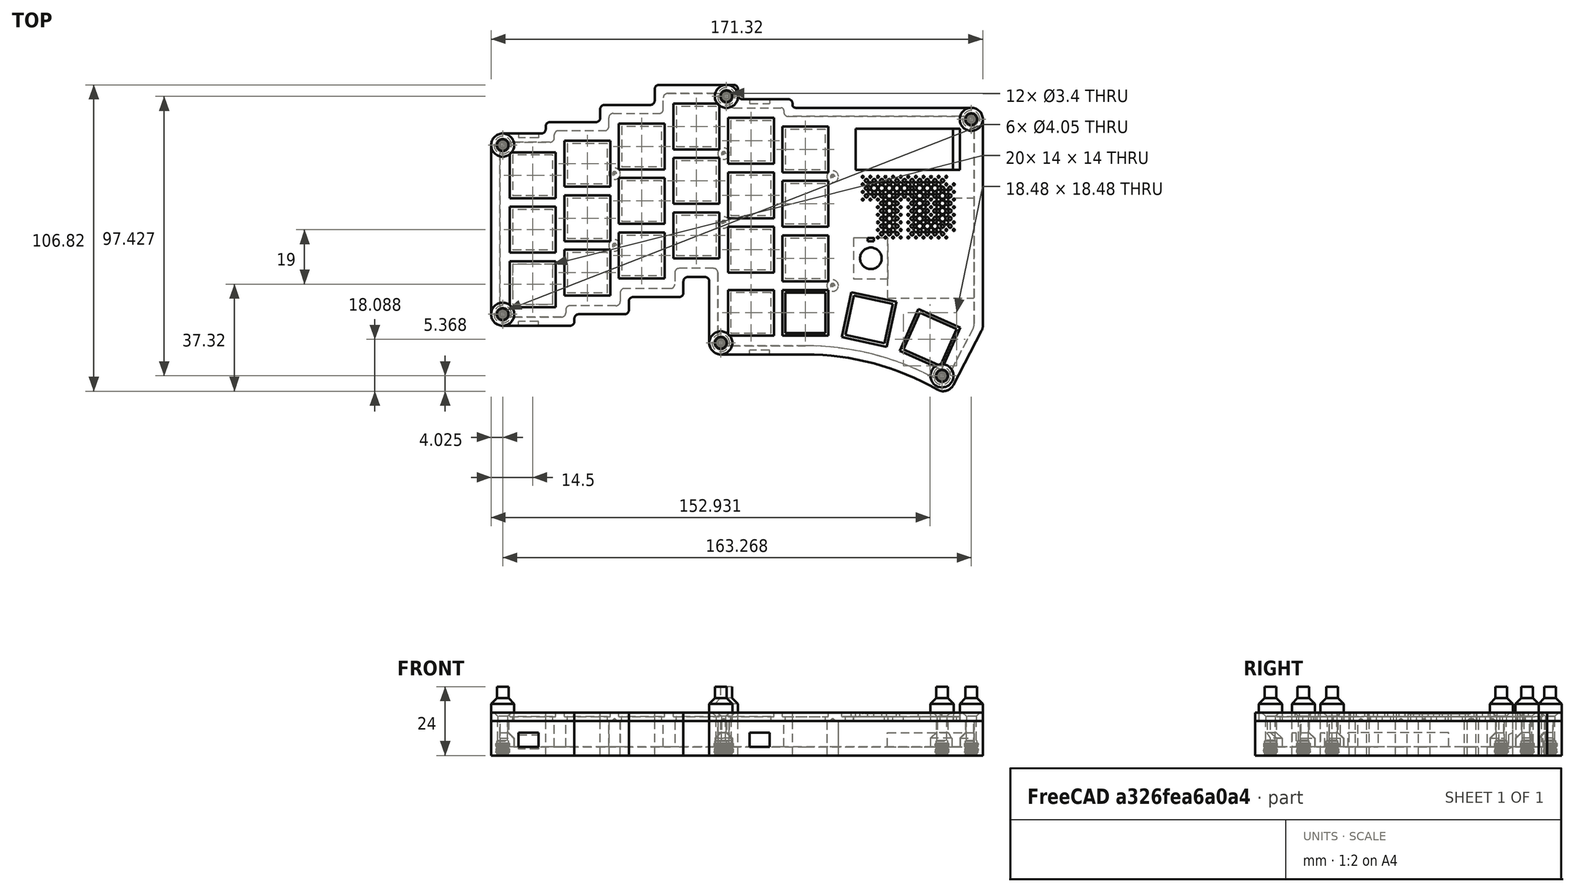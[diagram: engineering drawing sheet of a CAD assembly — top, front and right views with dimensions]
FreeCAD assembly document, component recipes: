
FREECAD ASSEMBLY — COMPONENT RECIPES ("LeftFrameTop")

This assembly document has 8 components, labeled P0..P7 below (a component is one placed body or linked part). 6 of them carry a construction recipe — the FreeCAD feature program that regenerates the part from scratch, quoted from this document or its linked companion documents; the rest are supplied as boundary geometry only. No exploded tour is included for this assembly.
COMPONENT P0 — recipe-attached ("SwitchPocket", modeled in this document).
Construction recipe (the document's own serialized feature program — sketch geometry with constraints, then the solid features built on it; lengths are millimeters unless a unit is written):

FEATURE [PartDesign::SubShapeBinder] Binder  label="FrameBorderBinder"
  BindCopyOnChange = 0
  BindMode = 0
  ClaimChildren = false
  Context = -> Body001 [Binder.]
  Fuse = false
  MakeFace = true
  OffsetFill = false
  OffsetIntersection = false
  OffsetJoinType = 0
  OffsetOpenResult = false
  PartialLoad = false
  Refine = true
  Relative = true
  Support = -> [Sketch002]
  _Version = 2
FEATURE [PartDesign::Pad] Pad
  Direction = (0,0,1)
  Length = 3
  Length2 = 10
  Profile = -> Binder
  Refine = true
  Suppressed = false
  Type = 0
  expr: Length = <<Config>>#<<Vars>>.PlateThickness
FEATURE [PartDesign::Fillet] Fillet
  Base = -> Pad [Edge38,Edge41,Edge44,Edge47,Edge50,Edge53,Edge56,Edge5,Edge11,Edge14,Edge8,Edge20,Edge17,Edge23,Edge26,Edge29]
  BaseFeature = -> Pad
  Radius = 1.5
  Refine = true
  SupportTransform = false
  Suppressed = false
  UseAllEdges = false
  expr: Radius = <<Config>>#<<Vars>>.MediumFillet
FEATURE [PartDesign::Fillet] Fillet001
  Base = -> Fillet [Edge119,Edge92,Edge88,Edge86,Edge46,Edge117]
  BaseFeature = -> Fillet
  Radius = 4
  Refine = true
  SupportTransform = false
  Suppressed = false
  UseAllEdges = false
  expr: Radius = <<Config>>#<<Vars>>.BigFillet
FEATURE [PartDesign::Fillet] Fillet002
  Base = -> Fillet001 [Edge48]
  BaseFeature = -> Fillet001
  Radius = 1
  Refine = true
  SupportTransform = false
  Suppressed = false
  UseAllEdges = false
  expr: Radius = <<Config>>#<<Vars>>.LittleFillet
FEATURE [PartDesign::Boolean] Boolean
  BaseFeature = -> Fillet002
  Group = -> [Array]
  Refine = true
  Suppressed = false
  Type = 1
  UsePlacement = true
FEATURE [PartDesign::Boolean] Boolean001
  BaseFeature = -> Boolean
  Group = -> [Binder002]
  Refine = true
  Suppressed = false
  Type = 1
  UsePlacement = true
FEATURE [PartDesign::Boolean] Boolean002
  BaseFeature = -> Boolean001
  Group = -> [Binder003]
  Refine = true
  Suppressed = false
  Type = 1
  UsePlacement = true
FEATURE [PartDesign::Boolean] Boolean003
  BaseFeature = -> Boolean002
  Group = -> [Binder004]
  Refine = true
  Suppressed = false
  Type = 1
  UsePlacement = true
FEATURE [PartDesign::SubShapeBinder] Binder009  label="M3HoleGeometryBinder"
  BindCopyOnChange = 0
  BindMode = 0
  ClaimChildren = false
  Context = -> Body001 [Binder009.]
  Fuse = false
  MakeFace = true
  OffsetFill = false
  OffsetIntersection = false
  OffsetJoinType = 0
  OffsetOpenResult = false
  PartialLoad = false
  Placement = pos=(0,0,3) rot=(0,0,1;0rad)
  Refine = true
  Relative = true
  Support = -> [PointArray003]
  _Version = 2
  expr: .Placement.Base.z = <<Config>>#<<Vars>>.PlateThickness
FEATURE [PartDesign::Hole] Hole
  BaseFeature = -> Boolean003
  CustomThreadClearance = 0
  Depth = 25
  DepthType = 0
  Diameter = 3.4
  DrillForDepth = false
  DrillPoint = 1
  DrillPointAngle = 118
  HoleCutCountersinkAngle = 90
  HoleCutCustomValues = false
  HoleCutDepth = 0
  HoleCutDiameter = 6.1
  HoleCutType = 2
  ModelThread = false
  Profile = -> Binder009
  Refine = true
  Suppressed = false
  Tapered = false
  TaperedAngle = 90
  ThreadClass = 0
  ThreadDepth = 25
  ThreadDepthType = 0
  ThreadDirection = 0
  ThreadFit = 0
  ThreadSize = 9
  ThreadType = 1
  Threaded = false
  UseCustomThreadClearance = false
FEATURE [PartDesign::Boolean] Boolean006
  BaseFeature = -> Hole
  Group = -> [Binder012]
  Refine = true
  Suppressed = false
  Type = 1
  UsePlacement = true
FEATURE [PartDesign::SubShapeBinder] Binder015
  BindCopyOnChange = 0
  BindMode = 0
  ClaimChildren = false
  Context = -> Body001 [Binder015.]
  Fuse = false
  MakeFace = true
  OffsetFill = false
  OffsetIntersection = false
  OffsetJoinType = 0
  OffsetOpenResult = false
  PartialLoad = false
  Placement = pos=(125.5,55.9,3) rot=(0,0,1;0rad)
  Refine = true
  Relative = true
  Support = -> [<external ../logo/Logo.FCStd>#Sketch]
  _Version = 2
  expr: .Placement.Base.z = <<Config>>#<<Vars>>.PlateThickness
FEATURE [PartDesign::Pocket] Pocket
  BaseFeature = -> Boolean006
  Direction = (0,0,-1)
  Length = 0.5
  Length2 = 5
  Profile = -> Binder015
  Refine = true
  Suppressed = false
  Type = 0
FEATURE [PartDesign::Body] Body001  label="FrameTop"
  AllowCompound = false
  Group = -> [Pad,Fillet,Fillet001,Fillet002,Binder,Boolean,Boolean001,Boolean002,Boolean003,Binder009,Hole,Boolean006,Binder015,Pocket]
  Origin = -> Origin001
  Tip = -> Pocket
COMPONENT P1 — same part as P0; its construction recipe is shown at P0.
COMPONENT P2 — geometry summary ("nice!nano v2 v1"; no construction recipe available for this part):
  bounding box: 34.2 x 17.8 x 3.3 mm
  tessellated surface: 61,186 triangles
  volume: 870 mm^3 (44% of its bounding box)
COMPONENT P3 — geometry summary ("EC11B-SW-Vert-F"; no construction recipe available for this part):
  bounding box: 25.4 x 14.9 x 12.0 mm
  tessellated surface: 43,648 triangles
  volume: 1468 mm^3 (32% of its bounding box)
COMPONENT P4 — recipe-attached ("RotaryPocket", a linked part whose construction recipe lives in a companion FreeCAD document of the same project; that document's serialized recipe follows).
Construction recipe (the companion document, serialized — sketch geometry with constraints, then the solid features built on it; lengths are millimeters unless a unit is written):

FCSTD DOCUMENT  (FreeCAD 1.0R39319 (Git))
Label: SwitchHoleNegative
License: All rights reserved
LicenseURL: https://en.wikipedia.org/wiki/All_rights_reserved
objects: Sketcher::SketchObject×7, PartDesign::Pad×7, PartDesign::Body×3, App::Link×1
note: 38 computed .brp shape members not serialized (recipe doc carries the construction recipe); baked Part::Feature solids carry a one-line shape summary decoded from their .brp
EXTERNAL_REF file=Config.FCStd obj=VarSet
EXTERNAL_REF file=lib/ec11.FCStd obj=EC11B_SW_Vert_F

FEATURE [Sketcher::SketchObject] Sketch001
  ArcFitTolerance = 1e-06
  AttachmentSupport = -> [XY_Plane003]
  FullyConstrained = true
  MakeInternals = false
  MapMode = 5
  expr: Constraints[8] = <<Config>>#<<Vars>>.SwitchHoleTotal
  expr: Constraints[9] = <<Config>>#<<Vars>>.SwitchHoleTotal
  sketch-geometry (4):
    g0: LineSegment StartX=7.025 StartY=-7.025 StartZ=0 EndX=7.025 EndY=7.025 EndZ=0
    g1: LineSegment StartX=7.025 StartY=7.025 StartZ=0 EndX=-7.025 EndY=7.025 EndZ=0
    g2: LineSegment StartX=-7.025 StartY=7.025 StartZ=0 EndX=-7.025 EndY=-7.025 EndZ=0
    g3: LineSegment StartX=-7.025 StartY=-7.025 StartZ=0 EndX=7.025 EndY=-7.025 EndZ=0
  constraints (11):
    c: Coincident(g0,g1)
    c: Coincident(g1,g2)
    c: Coincident(g2,g3)
    c: Coincident(g3,g0)
    c: Vertical(g0)
    c: Vertical(g2)
    c: Horizontal(g1)
    c: Horizontal(g3)
    c: DistanceX(g1,g1) = 14.05
    c: DistanceY(g2,g2) = 14.05
    c: Symmetric(g1,g0,g-1)
FEATURE [PartDesign::Pad] Pad001
  Direction = (0,0,1)
  Length = 1.5
  Length2 = 10
  Profile = -> Sketch001
  ReferenceAxis = -> Sketch001 [N_Axis]
  Refine = true
  Suppressed = false
  Type = 0
  expr: Length = <<Config>>#<<Vars>>.SwitchPlateThickness
FEATURE [Sketcher::SketchObject] Sketch002
  ArcFitTolerance = 1e-06
  AttachmentSupport = -> [Pad001]
  FullyConstrained = true
  MakeInternals = false
  MapMode = 5
  Placement = pos=(0,0,1.5) rot=(0,0,1;0rad)
  expr: Constraints[8] = <<Config>>#<<Vars>>.SwitchReliefLength
  expr: Constraints[9] = <<Config>>#<<Vars>>.SwitchReliefLength
  sketch-geometry (4):
    g0: LineSegment StartX=-8 StartY=8 StartZ=0 EndX=-8 EndY=-8 EndZ=0
    g1: LineSegment StartX=-8 StartY=-8 StartZ=0 EndX=8 EndY=-8 EndZ=0
    g2: LineSegment StartX=8 StartY=-8 StartZ=0 EndX=8 EndY=8 EndZ=0
    g3: LineSegment StartX=8 StartY=8 StartZ=0 EndX=-8 EndY=8 EndZ=0
  constraints (11):
    c: Coincident(g0,g1)
    c: Coincident(g1,g2)
    c: Coincident(g2,g3)
    c: Coincident(g3,g0)
    c: Vertical(g0)
    c: Vertical(g2)
    c: Horizontal(g1)
    c: Horizontal(g3)
    c: DistanceX(g3,g3) = 16
    c: DistanceY(g0,g0) = 16
    c: Symmetric(g0,g1,g-1)
FEATURE [PartDesign::Pad] Pad002
  BaseFeature = -> Pad001
  Direction = (0,0,1)
  Length = 1.5
  Length2 = 10
  Profile = -> Sketch002
  ReferenceAxis = -> Sketch002 [N_Axis]
  Refine = true
  Suppressed = false
  Type = 0
  expr: Length = <<Config>>#<<Vars>>.PlateThickness - <<Config>>#<<Vars>>.SwitchPlateThickness
FEATURE [PartDesign::Body] Body001  label="SwitchPocket"
  AllowCompound = false
  Group = -> [Sketch001,Pad001,Sketch002,Pad002]
  Origin = -> Origin003
  Placement = pos=(109.5,4.5,0) rot=(0,0,1;0rad)
  Tip = -> Pad002
FEATURE [Sketcher::SketchObject] Sketch
  ArcFitTolerance = 1e-06
  AttachmentSupport = -> [XY_Plane004]
  FullyConstrained = true
  MakeInternals = false
  MapMode = 5
  sketch-geometry (4):
    g0: LineSegment StartX=-6 StartY=-7.1 StartZ=0 EndX=6 EndY=-7.1 EndZ=0
    g1: LineSegment StartX=6 StartY=-7.1 StartZ=0 EndX=6 EndY=7.1 EndZ=0
    g2: LineSegment StartX=6 StartY=7.1 StartZ=0 EndX=-6 EndY=7.1 EndZ=0
    g3: LineSegment StartX=-6 StartY=7.1 StartZ=0 EndX=-6 EndY=-7.1 EndZ=0
  constraints (11):
    c: Coincident(g0,g1)
    c: Coincident(g1,g2)
    c: Coincident(g2,g3)
    c: Coincident(g3,g0)
    c: Horizontal(g0)
    c: Horizontal(g2)
    c: Vertical(g1)
    c: Vertical(g3)
    c: DistanceX(g2,g2) = 12
    c: DistanceY(g3,g3) = 14.2
    c: Symmetric(g2,g0,g-1)
FEATURE [App::Link] Link  label="EC11B-SW-Vert-F"
  LinkPlacement = pos=(0,-0.399999,-5) rot=(0,0,1;0rad)
  LinkedObject = -> <external lib/ec11.FCStd>#EC11B_SW_Vert_F
  Placement = pos=(0,-0.399999,-5) rot=(0,0,1;0rad)
FEATURE [PartDesign::Pad] Pad
  Direction = (0,0,1)
  Length = 1.5
  Length2 = 10
  Profile = -> Sketch
  ReferenceAxis = -> Sketch [N_Axis]
  Refine = true
  Suppressed = false
  Type = 0
  expr: Length = <<Config>>#<<Vars>>.PlateThickness - <<Config>>#<<Vars>>.SwitchPlateThickness
FEATURE [Sketcher::SketchObject] Sketch003
  ArcFitTolerance = 1e-06
  AttachmentSupport = -> [Pad]
  FullyConstrained = true
  MakeInternals = false
  MapMode = 5
  Placement = pos=(0,0,1.5) rot=(0,0,1;0rad)
  sketch-geometry (1):
    g0: Circle CenterX=0 CenterY=0 CenterZ=0 NormalX=0 NormalY=0 NormalZ=1 AngleXU=0 Radius=3.75
  constraints (2):
    c: Coincident(g0,g-1)
    c: Diameter(g0) = 7.5
FEATURE [PartDesign::Pad] Pad003
  BaseFeature = -> Pad
  Direction = (0,0,1)
  Length = 1.5
  Length2 = 10
  Profile = -> Sketch003
  ReferenceAxis = -> Sketch003 [N_Axis]
  Refine = true
  Suppressed = false
  Type = 0
  expr: Length = <<Config>>#<<Vars>>.SwitchPlateThickness
FEATURE [Sketcher::SketchObject] Sketch004
  ArcFitTolerance = 1e-06
  AttachmentSupport = -> [Pad003]
  ExternalGeometry = -> [Pad003]
  FullyConstrained = true
  MakeInternals = false
  MapMode = 5
  Placement = pos=(0,0,1.5) rot=(0,0,1;0rad)
  sketch-geometry (4):
    g0: LineSegment StartX=-1.075 StartY=-7.1 StartZ=0 EndX=1.075 EndY=-7.1 EndZ=0
    g1: LineSegment StartX=1.075 StartY=-7.1 StartZ=0 EndX=1.075 EndY=-5.9 EndZ=0
    g2: LineSegment StartX=1.075 StartY=-5.9 StartZ=0 EndX=-1.075 EndY=-5.9 EndZ=0
    g3: LineSegment StartX=-1.075 StartY=-5.9 StartZ=0 EndX=-1.075 EndY=-7.1 EndZ=0
  constraints (11):
    c: Coincident(g0,g1)
    c: Coincident(g1,g2)
    c: Coincident(g2,g3)
    c: Coincident(g3,g0)
    c: Horizontal(g0)
    c: Vertical(g1)
    c: Vertical(g3)
    c: PointOnObject(g0,g-3)
    c: Symmetric(g1,g2,g-2)
    c: Distance(g1,g3) = 2.15
    c: Distance(g0,g2) = 1.2
FEATURE [PartDesign::Pad] Pad004
  BaseFeature = -> Pad003
  Direction = (0,0,1)
  Length = 1.5
  Length2 = 10
  Profile = -> Sketch004
  ReferenceAxis = -> Sketch004 [N_Axis]
  Refine = true
  Suppressed = false
  Type = 0
  expr: Length = <<Config>>#<<Vars>>.SwitchPlateThickness
FEATURE [PartDesign::Body] Body003  label="RotaryPocket"
  AllowCompound = false
  Group = -> [Sketch,Pad,Sketch003,Pad003,Sketch004,Pad004]
  Origin = -> Origin004
  Tip = -> Pad004
FEATURE [Sketcher::SketchObject] Sketch005
  ArcFitTolerance = 1e-06
  AttachmentSupport = -> [XY_Plane]
  FullyConstrained = true
  MakeInternals = false
  MapMode = 5
  sketch-geometry (4):
    g0: LineSegment StartX=-7.15 StartY=-18.2 StartZ=0 EndX=7.15 EndY=-18.2 EndZ=0
    g1: LineSegment StartX=7.15 StartY=-18.2 StartZ=0 EndX=7.15 EndY=18.2 EndZ=0
    g2: LineSegment StartX=7.15 StartY=18.2 StartZ=0 EndX=-7.15 EndY=18.2 EndZ=0
    g3: LineSegment StartX=-7.15 StartY=18.2 StartZ=0 EndX=-7.15 EndY=-18.2 EndZ=0
  constraints (11):
    c: Coincident(g0,g1)
    c: Coincident(g1,g2)
    c: Coincident(g2,g3)
    c: Coincident(g3,g0)
    c: Horizontal(g0)
    c: Horizontal(g2)
    c: Vertical(g1)
    c: Vertical(g3)
    c: Symmetric(g2,g0,g-1)
    c: DistanceX(g2,g2) = 14.3
    c: DistanceY(g3,g3) = 36.4
FEATURE [PartDesign::Pad] Pad005
  Direction = (0,0,1)
  Length = 3
  Length2 = 10
  Profile = -> Sketch005
  ReferenceAxis = -> Sketch005 [N_Axis]
  Refine = true
  Suppressed = false
  Type = 0
FEATURE [Sketcher::SketchObject] Sketch006
  ArcFitTolerance = 1e-06
  AttachmentSupport = -> [Pad005]
  ExternalGeometry = -> [Pad005]
  FullyConstrained = true
  MakeInternals = false
  MapMode = 5
  Placement = pos=(0,0,0) rot=(1,0,0;3.14159rad)
  sketch-geometry (4):
    g0: LineSegment StartX=-7.15 StartY=18.2 StartZ=0 EndX=-7.15 EndY=15.8 EndZ=0
    g1: LineSegment StartX=-7.15 StartY=15.8 StartZ=0 EndX=7.15 EndY=15.8 EndZ=0
    g2: LineSegment StartX=7.15 StartY=15.8 StartZ=0 EndX=7.15 EndY=18.2 EndZ=0
    g3: LineSegment StartX=7.15 StartY=18.2 StartZ=0 EndX=-7.15 EndY=18.2 EndZ=0
  constraints (11):
    c: Coincident(g0,g1)
    c: Coincident(g1,g2)
    c: Coincident(g2,g3)
    c: Coincident(g3,g0)
    c: Vertical(g0)
    c: Vertical(g2)
    c: Horizontal(g1)
    c: Horizontal(g3)
    c: Coincident(g0,g-4)
    c: PointOnObject(g1,g-5)
    c: DistanceY(g2,g2) = 2.4
FEATURE [PartDesign::Pad] Pad006
  BaseFeature = -> Pad005
  Direction = (0,0,-1)
  Length = 1.5
  Length2 = 10
  Profile = -> Sketch006
  ReferenceAxis = -> Sketch006 [N_Axis]
  Refine = true
  Suppressed = false
  Type = 0
  expr: Length = <<Config>>#<<Vars>>.SwitchPlateThickness
FEATURE [PartDesign::Body] Body  label="NiceViewPocket"
  AllowCompound = false
  Group = -> [Sketch005,Pad005,Sketch006,Pad006]
  Origin = -> Origin
  Tip = -> Pad006
COMPONENT P5 — recipe-attached ("NiceViewPocket", modeled in this document).
Construction recipe (the document's own serialized feature program — sketch geometry with constraints, then the solid features built on it; lengths are millimeters unless a unit is written):

FEATURE [PartDesign::Body] Body  label="Layout"
  AllowCompound = false
  Origin = -> Origin
COMPONENT P6 — same part as P0; its construction recipe is shown at P0.
COMPONENT P7 — recipe-attached ("Support", modeled in this document).
Construction recipe (the document's own serialized feature program — sketch geometry with constraints, then the solid features built on it; lengths are millimeters unless a unit is written):

FEATURE [PartDesign::SubShapeBinder] Binder001  label="FrameBorderBinder001"
  BindCopyOnChange = 0
  BindMode = 0
  ClaimChildren = false
  Context = -> Body002 [Binder001.]
  Fuse = false
  MakeFace = true
  OffsetFill = false
  OffsetIntersection = false
  OffsetJoinType = 0
  OffsetOpenResult = false
  PartialLoad = false
  Placement = pos=(0,0,-12) rot=(0,0,1;0rad)
  Refine = true
  Relative = true
  Support = -> [Sketch002]
  _Version = 2
  expr: .Placement.Base.z = -<<Config>>#<<Vars>>.BottomCaseHeight
FEATURE [PartDesign::Pad] Pad001
  Direction = (0,0,1)
  Length = 12
  Length2 = 10
  Placement = pos=(0,0,-12) rot=(0,0,1;0rad)
  Profile = -> Binder001
  Refine = true
  Suppressed = false
  Type = 0
  expr: Length = <<Config>>#<<Vars>>.BottomCaseHeight
FEATURE [PartDesign::Thickness] Thickness
  Base = -> Pad001 [Face26]
  BaseFeature = -> Pad001
  Intersection = false
  Join = 1
  Mode = 0
  Refine = true
  Reversed = true
  SupportTransform = false
  Suppressed = false
  Value = 3
  expr: Value = <<Config>>#<<Vars>>.WallThickness
FEATURE [PartDesign::Fillet] Fillet003
  Base = -> Thickness [Edge35,Edge32,Edge65,Edge68,Edge1,Edge59,Edge118,Edge120,Edge136,Edge140,Edge97,Edge142]
  BaseFeature = -> Thickness
  Radius = 4
  Refine = true
  SupportTransform = false
  Suppressed = false
  UseAllEdges = false
  expr: Radius = <<Config>>#<<Vars>>.BigFillet
FEATURE [PartDesign::Fillet] Fillet004
  Base = -> Fillet003 [Edge120,Edge119,Edge117,Edge115,Edge113,Edge111,Edge109,Edge110,Edge108,Edge106,Edge104,Edge102,Edge100,Edge98,Edge96,Edge36,Edge158,Edge154,Edge150,Edge146,Edge142,Edge138,Edge134,Edge130,Edge122,Edge157,Edge161,Edge165,Edge169,Edge173,Edge177,Edge179]
  BaseFeature = -> Fillet003
  Radius = 1.5
  Refine = true
  SupportTransform = false
  Suppressed = false
  UseAllEdges = false
  expr: Radius = <<Config>>#<<Vars>>.MediumFillet
FEATURE [PartDesign::Fillet] Fillet005
  Base = -> Fillet004 [Edge48,Edge193]
  BaseFeature = -> Fillet004
  Radius = 1
  Refine = true
  SupportTransform = false
  Suppressed = false
  UseAllEdges = false
  expr: Radius = <<Config>>#<<Vars>>.LittleFillet
FEATURE [PartDesign::Boolean] Boolean007
  BaseFeature = -> Fillet005
  Group = -> [Binder008]
  Refine = true
  Suppressed = false
  Type = 0
  UsePlacement = true
FEATURE [PartDesign::SubShapeBinder] Binder013  label="HolesGeometryBinder"
  BindCopyOnChange = 0
  BindMode = 0
  ClaimChildren = false
  Context = -> Body002 [Binder013.]
  Fuse = false
  MakeFace = true
  OffsetFill = false
  OffsetIntersection = false
  OffsetJoinType = 0
  OffsetOpenResult = false
  PartialLoad = false
  Placement = pos=(0,0,-12) rot=(0,0,1;0rad)
  Refine = true
  Relative = true
  Support = -> [PointArray003]
  _Version = 2
  expr: .Placement.Base.z = -<<Config>>#<<Vars>>.BottomCaseHeight
FEATURE [PartDesign::Hole] Hole001
  BaseFeature = -> Boolean007
  CustomThreadClearance = 0
  Depth = 25
  DepthType = 0
  Diameter = 3.4
  DrillForDepth = false
  DrillPoint = 1
  DrillPointAngle = 118
  HoleCutCountersinkAngle = 90
  HoleCutCustomValues = false
  HoleCutDepth = 5
  HoleCutDiameter = 4.05
  HoleCutType = 3
  ModelThread = false
  Profile = -> Binder013
  Refine = true
  Reversed = true
  Suppressed = false
  Tapered = false
  TaperedAngle = 90
  ThreadClass = 0
  ThreadDepth = 25
  ThreadDepthType = 0
  ThreadDirection = 0
  ThreadFit = 0
  ThreadSize = 9
  ThreadType = 1
  Threaded = false
  UseCustomThreadClearance = false
  expr: HoleCutDepth = <<Config>>#<<Vars>>.M3InsertLength
  expr: HoleCutDiameter = <<Config>>#<<Vars>>.M3InsertDiameter
FEATURE [PartDesign::Boolean] Boolean008
  BaseFeature = -> Hole001
  Group = -> [Binder014]
  Refine = true
  Suppressed = false
  Type = 0
  UsePlacement = true
FEATURE [Sketcher::SketchObject] Sketch006
  ArcFitTolerance = 1e-06
  AttachmentSupport = -> [Boolean008]
  FullyConstrained = true
  MakeInternals = false
  MapMode = 5
  Placement = pos=(0,-10,0) rot=(1,0,0;1.5708rad)
  expr: Constraints[10] = <<Config>>#<<Vars>>.AddonSlotPosZ
  expr: Constraints[11] = <<Config>>#<<Vars>>.AddonSlot2PosX
  expr: Constraints[8] = <<Config>>#<<Vars>>.AddonSlotWidth
  expr: Constraints[9] = <<Config>>#<<Vars>>.AddonSlotHeight
  sketch-geometry (4):
    g0: LineSegment StartX=90 StartY=3 StartZ=0 EndX=97 EndY=3 EndZ=0
    g1: LineSegment StartX=97 StartY=3 StartZ=0 EndX=97 EndY=8 EndZ=0
    g2: LineSegment StartX=97 StartY=8 StartZ=0 EndX=90 EndY=8 EndZ=0
    g3: LineSegment StartX=90 StartY=8 StartZ=0 EndX=90 EndY=3 EndZ=0
  constraints (12):
    c: Coincident(g0,g1)
    c: Coincident(g1,g2)
    c: Coincident(g2,g3)
    c: Coincident(g3,g0)
    c: Horizontal(g0)
    c: Horizontal(g2)
    c: Vertical(g1)
    c: Vertical(g3)
    c: DistanceX(g0,g0) = 7
    c: DistanceY(g3,g3) = 5
    c: Distance(g-1,g0) = 3
    c: Distance(g-2,g3) = 90
FEATURE [PartDesign::Pocket] Pocket001
  BaseFeature = -> Boolean008
  Direction = (0,1,-2e-16)
  Length = 1.5
  Length2 = 5
  Profile = -> Sketch006
  ReferenceAxis = -> Sketch006 [N_Axis]
  Refine = true
  Suppressed = false
  Type = 0
FEATURE [Sketcher::SketchObject] Sketch007
  ArcFitTolerance = 1e-06
  AttachmentSupport = -> [Pocket001]
  FullyConstrained = true
  MakeInternals = false
  MapMode = 5
  Placement = pos=(0,79,0) rot=(0,0.707107,0.707107;3.14159rad)
  expr: Constraints[10] = <<Config>>#<<Vars>>.AddonSlotPosZ
  expr: Constraints[11] = <<Config>>#<<Vars>>.AddonSlot2PosX
  expr: Constraints[8] = <<Config>>#<<Vars>>.AddonSlotWidth
  expr: Constraints[9] = <<Config>>#<<Vars>>.AddonSlotHeight
  sketch-geometry (4):
    g0: LineSegment StartX=-97 StartY=8 StartZ=0 EndX=-97 EndY=3 EndZ=0
    g1: LineSegment StartX=-97 StartY=3 StartZ=0 EndX=-90 EndY=3 EndZ=0
    g2: LineSegment StartX=-90 StartY=3 StartZ=0 EndX=-90 EndY=8 EndZ=0
    g3: LineSegment StartX=-90 StartY=8 StartZ=0 EndX=-97 EndY=8 EndZ=0
  constraints (12):
    c: Coincident(g0,g1)
    c: Coincident(g1,g2)
    c: Coincident(g2,g3)
    c: Coincident(g3,g0)
    c: Vertical(g0)
    c: Vertical(g2)
    c: Horizontal(g1)
    c: Horizontal(g3)
    c: DistanceX(g1,g1) = 7
    c: DistanceY(g0,g0) = 5
    c: Distance(g-1,g1) = 3
    c: Distance(g-2,g2) = 90
FEATURE [PartDesign::Pocket] Pocket002
  BaseFeature = -> Pocket001
  Direction = (0,-1,2e-16)
  Length = 1.5
  Length2 = 5
  Profile = -> Sketch007
  ReferenceAxis = -> Sketch007 [N_Axis]
  Refine = true
  Suppressed = false
  Type = 0
  expr: Length = <<Config>>#<<Vars>>.AddonSlotDepth
FEATURE [Sketcher::SketchObject] Sketch008
  ArcFitTolerance = 1e-06
  AttachmentSupport = -> [Pocket002]
  FullyConstrained = true
  MakeInternals = false
  MapMode = 5
  Placement = pos=(0,0,0) rot=(1,0,0;1.5708rad)
  expr: Constraints[10] = <<Config>>#<<Vars>>.AddonSlotPosZ
  expr: Constraints[11] = <<Config>>#<<Vars>>.AddonSlot1PosX
  expr: Constraints[8] = <<Config>>#<<Vars>>.AddonSlotWidth
  expr: Constraints[9] = <<Config>>#<<Vars>>.AddonSlotHeight
  sketch-geometry (4):
    g0: LineSegment StartX=9.5 StartY=8 StartZ=0 EndX=9.5 EndY=3 EndZ=0
    g1: LineSegment StartX=9.5 StartY=3 StartZ=0 EndX=16.5 EndY=3 EndZ=0
    g2: LineSegment StartX=16.5 StartY=3 StartZ=0 EndX=16.5 EndY=8 EndZ=0
    g3: LineSegment StartX=16.5 StartY=8 StartZ=0 EndX=9.5 EndY=8 EndZ=0
  constraints (12):
    c: Coincident(g0,g1)
    c: Coincident(g1,g2)
    c: Coincident(g2,g3)
    c: Coincident(g3,g0)
    c: Vertical(g0)
    c: Vertical(g2)
    c: Horizontal(g1)
    c: Horizontal(g3)
    c: DistanceX(g1,g1) = 7
    c: DistanceY(g2,g2) = 5
    c: Distance(g-1,g1) = 3
    c: Distance(g-2,g0) = 9.5
FEATURE [PartDesign::Pocket] Pocket003
  BaseFeature = -> Pocket002
  Direction = (0,1,-2e-16)
  Length = 1.5
  Length2 = 5
  Profile = -> Sketch008
  ReferenceAxis = -> Sketch008 [N_Axis]
  Refine = true
  Suppressed = false
  Type = 0
  expr: Length = <<Config>>#<<Vars>>.AddonSlotDepth
FEATURE [Sketcher::SketchObject] Sketch009
  ArcFitTolerance = 1e-06
  AttachmentSupport = -> [Pocket003]
  FullyConstrained = true
  MakeInternals = false
  MapMode = 5
  Placement = pos=(0,67,0) rot=(0,0.707107,0.707107;3.14159rad)
  expr: Constraints[10] = <<Config>>#<<Vars>>.AddonSlotPosZ
  expr: Constraints[11] = <<Config>>#<<Vars>>.AddonSlot1PosX
  expr: Constraints[8] = <<Config>>#<<Vars>>.AddonSlotHeight
  expr: Constraints[9] = <<Config>>#<<Vars>>.AddonSlotWidth
  sketch-geometry (4):
    g0: LineSegment StartX=-9.5 StartY=3 StartZ=0 EndX=-9.5 EndY=8 EndZ=0
    g1: LineSegment StartX=-9.5 StartY=8 StartZ=0 EndX=-16.5 EndY=8 EndZ=0
    g2: LineSegment StartX=-16.5 StartY=8 StartZ=0 EndX=-16.5 EndY=3 EndZ=0
    g3: LineSegment StartX=-16.5 StartY=3 StartZ=0 EndX=-9.5 EndY=3 EndZ=0
  constraints (12):
    c: Coincident(g0,g1)
    c: Coincident(g1,g2)
    c: Coincident(g2,g3)
    c: Coincident(g3,g0)
    c: Vertical(g0)
    c: Vertical(g2)
    c: Horizontal(g1)
    c: Horizontal(g3)
    c: DistanceY(g0,g0) = 5
    c: DistanceX(g3,g3) = 7
    c: Distance(g-1,g3) = 3
    c: Distance(g-2,g0) = 9.5
FEATURE [PartDesign::Pocket] Pocket004
  BaseFeature = -> Pocket003
  Direction = (0,-1,-0.5)
  Length = 1.5
  Length2 = 5
  Profile = -> Sketch009
  ReferenceAxis = -> Sketch009 [N_Axis]
  Refine = true
  Suppressed = false
  Type = 0
  UseCustomVector = true
  expr: Length = <<Config>>#<<Vars>>.AddonSlotDepth
FEATURE [PartDesign::Body] Body002  label="FrameBottom"
  AllowCompound = false
  Group = -> [Binder001,Pad001,Thickness,Fillet003,Fillet004,Fillet005,Boolean007,Binder013,Hole001,Boolean008,Sketch006,Pocket001,Sketch007,Pocket002,Sketch008,Pocket003,Sketch009,Pocket004]
  Origin = -> Origin002
  Placement = pos=(0,0,-12) rot=(0,0,1;0rad)
  Tip = -> Pocket004
  expr: .Placement.Base.z = -<<Config>>#<<Vars>>.BottomCaseHeight
PROVENANCE & LICENSES
A FreeCAD (.FCStd) document from a public repository crawl; recipes are the document's own serialized feature recipes (and, for linked parts, companion documents' recipes).
License: mit.
